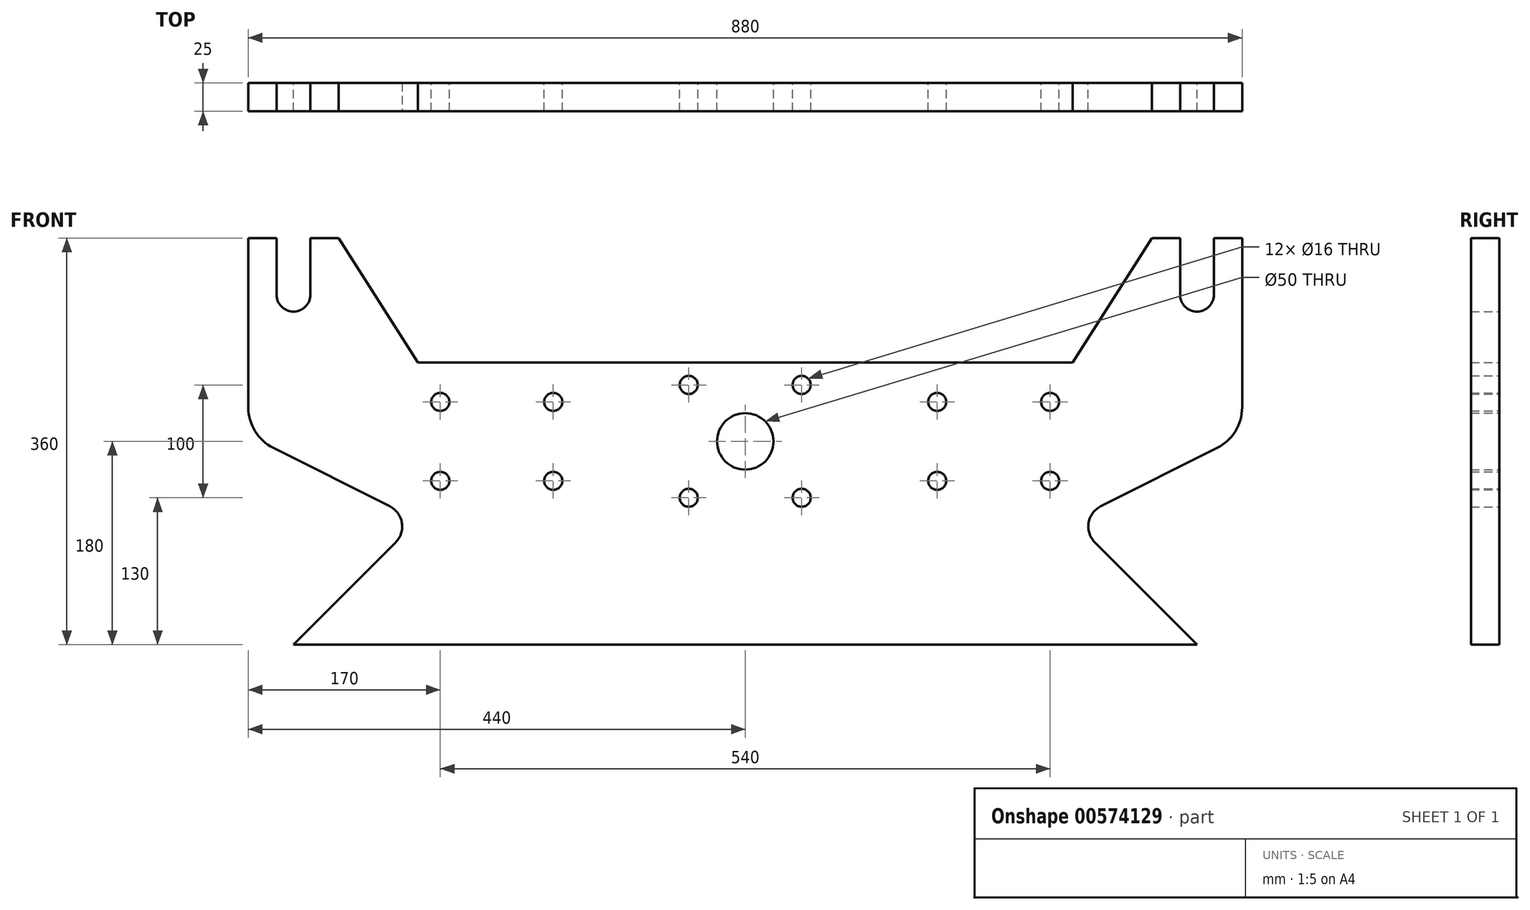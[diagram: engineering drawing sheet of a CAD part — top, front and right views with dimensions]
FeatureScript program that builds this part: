
annotation { "Feature Type Name" : "Feature", "Feature Type Description" : "" }
export const myFeature = defineFeature(function(context is Context, id is Id, definition is map)
    precondition{}
    {
        {
            var Q0;
            Q0=qCreatedBy(makeId("Front.planeOp"),FACE);
            var sketch = newSketch(context, id + "F0", { "sketchPlane" : qUnion([Q0])});
            skLineSegment(sketch, "E0", {"start": v(-290, 140) * mm, "end": v(290, 140) * mm});
            skLineSegment(sketch, "E1", {"start": v(290, 140) * mm, "end": v(290, 0) * mm});
            skLineSegment(sketch, "E2", {"start": v(290, 0) * mm, "end": v(400, -110) * mm});
            skLineSegment(sketch, "E3", {"start": v(400, -110) * mm, "end": v(-400, -110) * mm});
            skLineSegment(sketch, "E4", {"start": v(-400, -110) * mm, "end": v(-290, 0) * mm});
            skLineSegment(sketch, "E5", {"start": v(-290, 0) * mm, "end": v(-290, 140) * mm});
            skLineSegment(sketch, "E6", {"start": v(-290, 0) * mm, "end": v(290, 0) * mm});
            skLineSegment(sketch, "E7", {"start": v(-290, 105) * mm, "end": v(290, 105) * mm, "construction": true});
            skLineSegment(sketch, "E8", {"start": v(-290, 35) * mm, "end": v(290, 35) * mm, "construction": true});
            skCircle(sketch, "E9", {"center": v(-270, 105) * mm, "radius": 8 * mm});
            skCircle(sketch, "E10", {"center": v(-170, 105) * mm, "radius": 8 * mm});
            skCircle(sketch, "E11", {"center": v(-270, 35) * mm, "radius": 8 * mm});
            skCircle(sketch, "E12", {"center": v(-170, 35) * mm, "radius": 8 * mm});
            skCircle(sketch, "E13", {"center": v(270, 105) * mm, "radius": 8 * mm});
            skCircle(sketch, "E14", {"center": v(270, 35) * mm, "radius": 8 * mm});
            skCircle(sketch, "E15", {"center": v(170, 105) * mm, "radius": 8 * mm});
            skCircle(sketch, "E16", {"center": v(170, 35) * mm, "radius": 8 * mm});
            skCircle(sketch, "E17", {"center": v(0, 70) * mm, "radius": 25 * mm});
            skCircle(sketch, "E18", {"center": v(50, 120) * mm, "radius": 8 * mm});
            skCircle(sketch, "E19", {"center": v(-50, 120) * mm, "radius": 8 * mm});
            skCircle(sketch, "E20", {"center": v(-50, 20) * mm, "radius": 8 * mm});
            skCircle(sketch, "E21", {"center": v(50, 20) * mm, "radius": 8 * mm});
            skLineSegment(sketch, "E22", {"start": v(-533.23, 100) * mm, "end": v(572.06, 100) * mm, "construction": true});
            skArc(sketch, "E23", {"start": v(-440, 100) * mm, "mid": v(-434.04, 79) * mm, "end": v(-417.95, 64.25) * mm});
            skArc(sketch, "E24", {"start": v(417.95, 64.25) * mm, "mid": v(434.04, 79) * mm, "end": v(440, 100) * mm});
            skLineSegment(sketch, "E25", {"start": v(-290, 0) * mm, "end": v(-417.95, 64.25) * mm});
            skLineSegment(sketch, "E26", {"start": v(290, 0) * mm, "end": v(417.95, 64.25) * mm});
            skLineSegment(sketch, "E27", {"start": v(-440, 100) * mm, "end": v(-440, 250) * mm});
            skLineSegment(sketch, "E28", {"start": v(-290, 140) * mm, "end": v(-360, 250) * mm});
            skLineSegment(sketch, "E29", {"start": v(-440, 250) * mm, "end": v(-415, 250) * mm});
            skLineSegment(sketch, "E30", {"start": v(-415, 200) * mm, "end": v(-415, 250) * mm});
            skLineSegment(sketch, "E31", {"start": v(-385, 200) * mm, "end": v(-385, 250) * mm});
            skLineSegment(sketch, "E32", {"start": v(-533.23, 200) * mm, "end": v(-440, 200) * mm});
            skArc(sketch, "E33", {"start": v(-415, 200) * mm, "mid": v(-400, 185) * mm, "end": v(-385, 200) * mm});
            skLineSegment(sketch, "E34.trimOffspring", {"start": v(-385, 250) * mm, "end": v(-360, 250) * mm});
            skLineSegment(sketch, "E35.trimOffspring", {"start": v(-328.18, 200) * mm, "end": v(328.18, 200) * mm});
            skPoint(sketch, "E36.start.orphan", {"position": v(-533.23, 115) * mm});
            skLineSegment(sketch, "E37", {"start": v(440, 100) * mm, "end": v(440, 250) * mm});
            skLineSegment(sketch, "E38", {"start": v(360, 250) * mm, "end": v(290, 140) * mm});
            skLineSegment(sketch, "E39.trimOffspring", {"start": v(440, 200) * mm, "end": v(572.06, 200) * mm});
            skPoint(sketch, "E40.start.orphan", {"position": v(385, 250) * mm});
            skPoint(sketch, "E41.center.orphan", {"position": v(400, 200) * mm});
            skPoint(sketch, "E42.start.orphan", {"position": v(415, 250) * mm});
            skLineSegment(sketch, "E43", {"start": v(440, 250) * mm, "end": v(415, 250) * mm});
            skLineSegment(sketch, "E44", {"start": v(385, 250) * mm, "end": v(360, 250) * mm});
            skLineSegment(sketch, "E45", {"start": v(385, 250) * mm, "end": v(385, 200) * mm});
            skLineSegment(sketch, "E46", {"start": v(415, 200) * mm, "end": v(415, 250) * mm});
            skArc(sketch, "E47", {"start": v(385, 200) * mm, "mid": v(400, 185) * mm, "end": v(415, 200) * mm});
            skSolve(sketch);
        }
        {
            var Q0;
            Q0=makeQuery(id+"F0.imprint","IMPRINT",FACE,{"disambiguationData":[TD([[makeQuery(id+"F0.imprint","IMPRINT",EDGE,{"derivedFrom":sQuery(id+"F0.wireOp",EDGE,"E0")}),-1.0]])]});
            var Q1;
            Q1=makeQuery(id+"F0.imprint","IMPRINT",FACE,{"disambiguationData":[TD([[makeQuery(id+"F0.imprint","IMPRINT",EDGE,{"derivedFrom":sQuery(id+"F0.wireOp",EDGE,"E5")}),1.0]])]});
            var Q2;
            Q2=makeQuery(id+"F0.imprint","IMPRINT",FACE,{"disambiguationData":[TD([[makeQuery(id+"F0.imprint","IMPRINT",EDGE,{"derivedFrom":sQuery(id+"F0.wireOp",EDGE,"tXtaD7kT-JV7T-NhUJ-hU74-hw88XEuNJVRT")}),-1.0]])]});
            var Q3;
            Q3=makeQuery(id+"F0.imprint","IMPRINT",FACE,{"disambiguationData":[TD([[makeQuery(id+"F0.imprint","IMPRINT",EDGE,{"derivedFrom":sQuery(id+"F0.wireOp",EDGE,"E2")}),-1.0]])]});
            var Q4;
            Q4=makeQuery(id+"F0.imprint","IMPRINT",FACE,{"disambiguationData":[TD([[makeQuery(id+"F0.imprint","IMPRINT",EDGE,{"derivedFrom":sQuery(id+"F0.wireOp",EDGE,"E1")}),1.0]])]});
            var Q5;
            Q5=makeQuery(id+"F0.imprint","IMPRINT",FACE,{"disambiguationData":[TD([[makeQuery(id+"F0.imprint","IMPRINT",EDGE,{"derivedFrom":sQuery(id+"F0.wireOp",EDGE,"6735OMPZ-TfTd-i0L7-MPv8-s5K211O1Ho69")}),-1.0]])]});
            extrude(context, id + "F1", {"entities" : qUnion([Q0, Q1, Q2, Q3, Q4, Q5]), "depth" : 25 * mm, "offsetDistance" : 25 * mm});
        }
        {
            var Q0;
            Q0=makeQuery(id+"F1.opExtrude","SWEPT_EDGE",EDGE,{"disambiguationData":[OSD([sQuery(id+"F0.wireOp",EDGE,"E4"),sQuery(id+"F0.wireOp",EDGE,"E5"),sQuery(id+"F0.wireOp",EDGE,"E6"),sQuery(id+"F0.wireOp",EDGE,"E25")])]});
            var Q1;
            Q1=makeQuery(id+"F1.opExtrude","SWEPT_EDGE",EDGE,{"disambiguationData":[OSD([sQuery(id+"F0.wireOp",EDGE,"E1"),sQuery(id+"F0.wireOp",EDGE,"E2"),sQuery(id+"F0.wireOp",EDGE,"E6"),sQuery(id+"F0.wireOp",EDGE,"E26")])]});
            fillet(context, id + "F2", {"entities" : qUnion([Q0, Q1]), "radius" : 20 * mm, "tangentPropagation" : true, "allowEdgeOverflow" : false});
        }
    });
